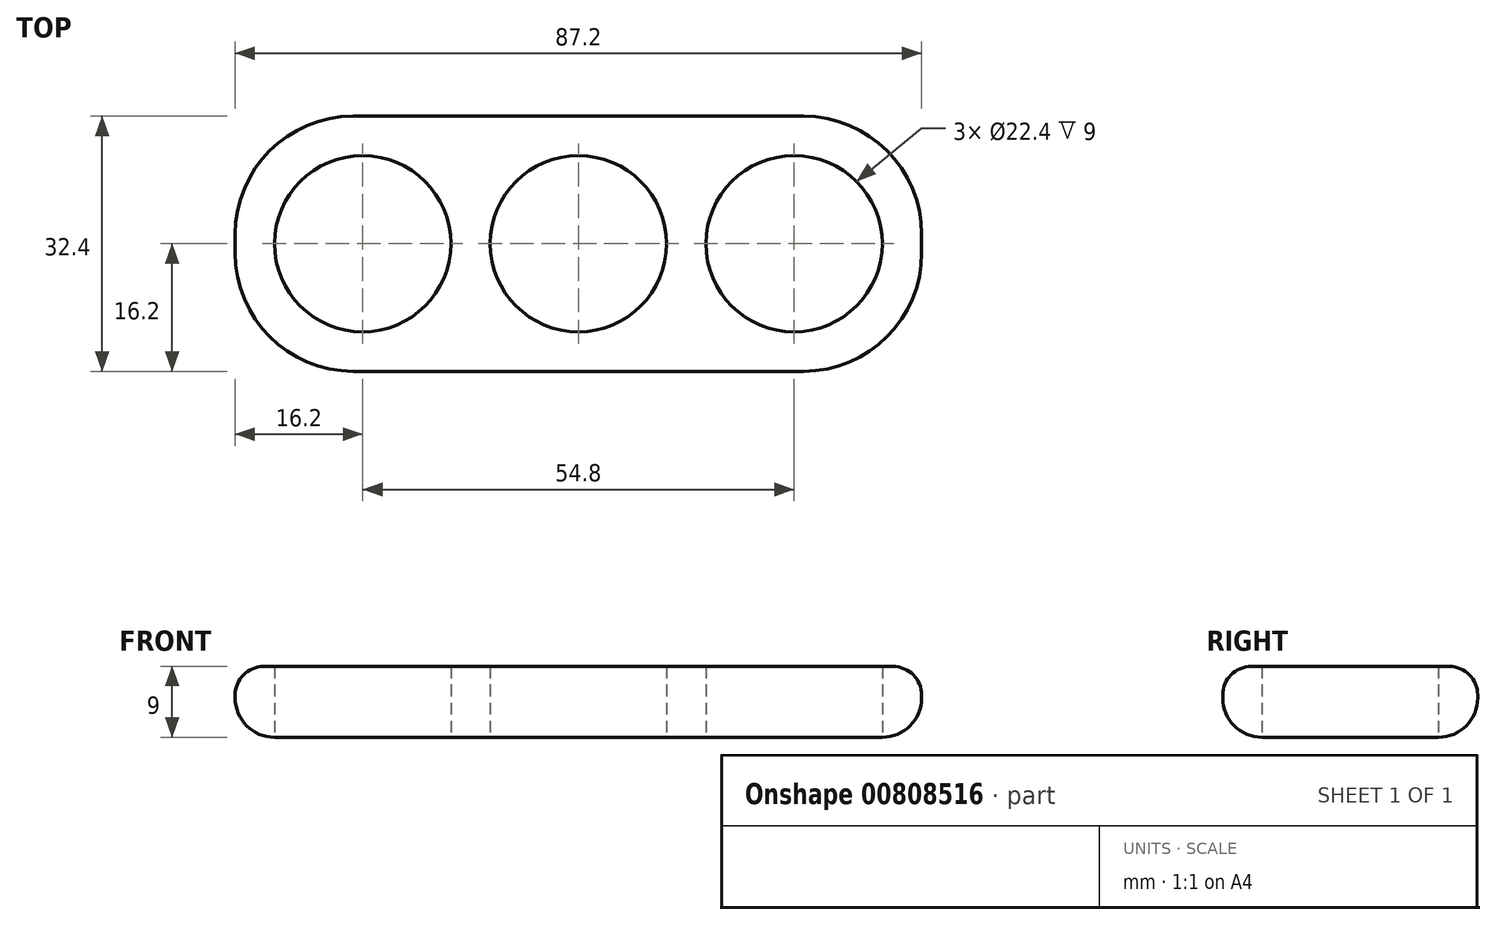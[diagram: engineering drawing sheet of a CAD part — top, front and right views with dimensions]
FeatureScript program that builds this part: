
annotation { "Feature Type Name" : "Feature", "Feature Type Description" : "" }
export const myFeature = defineFeature(function(context is Context, id is Id, definition is map)
    precondition{}
    {
        {
            var Q0;
            Q0=qCreatedBy(makeId("Top.planeOp"),FACE);
            var sketch = newSketch(context, id + "F0", { "sketchPlane" : qUnion([Q0])});
            skCircle(sketch, "E0", {"center": v(0, 0) * mm, "radius": 11.2 * mm});
            skCircle(sketch, "E1", {"center": v(27.4, 0) * mm, "radius": 11.2 * mm});
            skCircle(sketch, "E2", {"center": v(-27.4, 0) * mm, "radius": 11.2 * mm});
            skLineSegment(sketch, "E3.bottom", {"start": v(-28.6, 16.2) * mm, "end": v(28.6, 16.2) * mm});
            skLineSegment(sketch, "E3.top", {"start": v(-28.6, -16.2) * mm, "end": v(28.6, -16.2) * mm});
            skLineSegment(sketch, "E3.left", {"start": v(-43.6, 1.2) * mm, "end": v(-43.6, -1.2) * mm});
            skLineSegment(sketch, "E3.right", {"start": v(43.6, 1.2) * mm, "end": v(43.6, -1.2) * mm});
            skPoint(sketch, "E4.visualSharp", {"position": v(-43.6, 16.2) * mm});
            skArc(sketch, "E4.filletArc", {"start": v(-28.6, 16.2) * mm, "mid": v(-39.2, 11.8) * mm, "end": v(-43.6, 1.2) * mm});
            skPoint(sketch, "E5.visualSharp", {"position": v(-43.6, -16.2) * mm});
            skArc(sketch, "E5.filletArc", {"start": v(-43.6, -1.2) * mm, "mid": v(-39.2, -11.8) * mm, "end": v(-28.6, -16.2) * mm});
            skPoint(sketch, "E6.visualSharp", {"position": v(43.6, -16.2) * mm});
            skArc(sketch, "E6.filletArc", {"start": v(28.6, -16.2) * mm, "mid": v(39.2, -11.8) * mm, "end": v(43.6, -1.2) * mm});
            skPoint(sketch, "E7.visualSharp", {"position": v(43.6, 16.2) * mm});
            skArc(sketch, "E7.filletArc", {"start": v(43.6, 1.2) * mm, "mid": v(39.2, 11.8) * mm, "end": v(28.6, 16.2) * mm});
            skSolve(sketch);
        }
        {
            var Q0;
            Q0=makeQuery(id+"F0.imprint","IMPRINT",FACE,{"disambiguationData":[TD([[makeQuery(id+"F0.imprint","IMPRINT",EDGE,{"derivedFrom":sQuery(id+"F0.wireOp",EDGE,"E0")}),-1.0]])]});
            extrude(context, id + "F1", {"entities" : qUnion([Q0]), "depth" : 9 * mm, "offsetDistance" : 25 * mm});
        }
        {
            var Q0;
            Q0=makeQuery(id+"F1.opExtrude","CAP_EDGE",EDGE,{"disambiguationData":[OSD([sQuery(id+"F0.wireOp",EDGE,"E7.filletArc")])],"isStart":false});
            fillet(context, id + "F2", {"entities" : qUnion([Q0]), "radius" : 3.62 * mm, "tangentPropagation" : true, "allowEdgeOverflow" : false});
        }
        {
            var Q0;
            Q0=makeQuery(id+"F1.opExtrude","CAP_EDGE",EDGE,{"disambiguationData":[OSD([sQuery(id+"F0.wireOp",EDGE,"E3.bottom")])],"isStart":true});
            var Q1;
            Q1=makeQuery(id+"F1.opExtrude","CAP_EDGE",EDGE,{"disambiguationData":[OSD([sQuery(id+"F0.wireOp",EDGE,"E7.filletArc")])],"isStart":true});
            fillet(context, id + "F3", {"entities" : qUnion([Q0, Q1]), "radius" : 5 * mm, "tangentPropagation" : true, "allowEdgeOverflow" : false});
        }
    });
